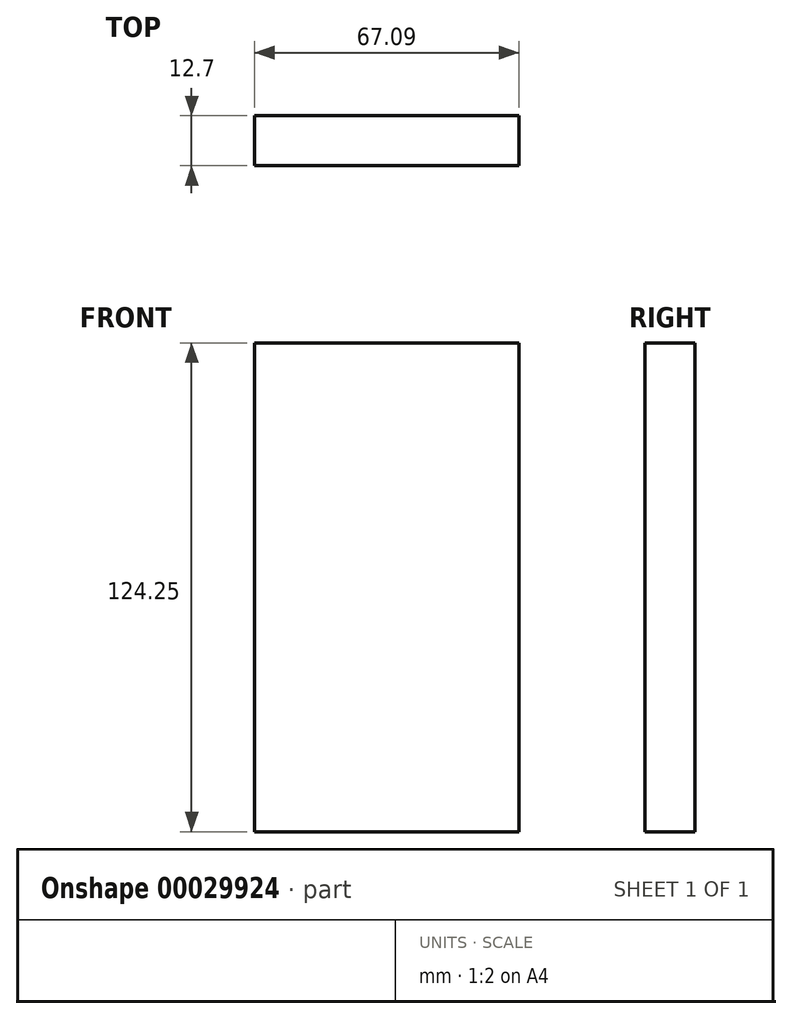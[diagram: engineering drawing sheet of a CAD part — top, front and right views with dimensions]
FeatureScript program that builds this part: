
annotation { "Feature Type Name" : "Feature", "Feature Type Description" : "" }
export const myFeature = defineFeature(function(context is Context, id is Id, definition is map)
    precondition{}
    {
        {
            var Q0;
            Q0=qCreatedBy(makeId("Front.planeOp"),FACE);
            var sketch = newSketch(context, id + "F0", { "sketchPlane" : qUnion([Q0])});
            skLineSegment(sketch, "E0.bottom", {"start": v(-67.1, 63.69) * mm, "end": v(0, 63.69) * mm});
            skLineSegment(sketch, "E0.top", {"start": v(-67.1, -60.56) * mm, "end": v(0, -60.56) * mm});
            skLineSegment(sketch, "E0.left", {"start": v(-67.1, 63.69) * mm, "end": v(-67.1, -60.56) * mm});
            skLineSegment(sketch, "E0.right", {"start": v(0, 63.69) * mm, "end": v(0, -60.56) * mm});
            skSolve(sketch);
        }
        {
            var Q0;
            Q0=makeQuery(id+"F0.imprint","IMPRINT",FACE,{"disambiguationData":[TD([[makeQuery(id+"F0.imprint","IMPRINT",EDGE,{"derivedFrom":sQuery(id+"F0.wireOp",EDGE,"E0.bottom")}),-1.0]])]});
            extrude(context, id + "F1", {"entities" : qUnion([Q0]), "depth" : 12.7 * mm});
        }
    });
